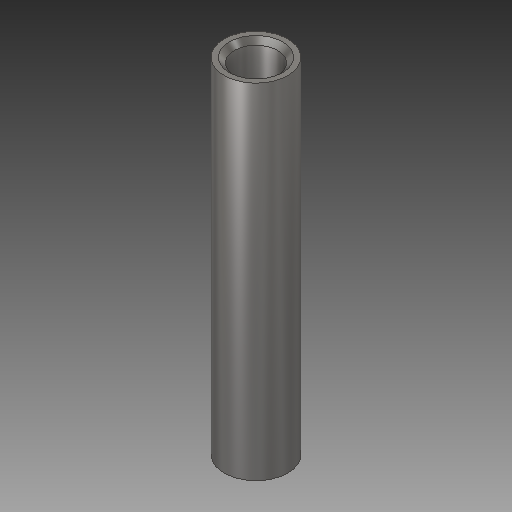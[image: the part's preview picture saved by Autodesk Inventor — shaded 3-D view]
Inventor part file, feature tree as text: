
AUTODESK INVENTOR PART (.ipt)
format: ipt  version: 2018.2 (Build 222227000, 227)  size: 106,496 bytes
history: native  units: mm
features: extrude x1, chamfer x1, sketch x1
ambient origin geometry x8: Origin, YZ Plane, XZ Plane, XY Plane, X Axis, Y Axis, Z Axis, Center Point
bodies: Solid1 (feature_tree)
feature tree (3):
  extrude  "Extrusion1"  Depth=52.0mm
  chamfer  "Chamfer1"  Distance=52.0mm
  sketch  "Sketch1"  dims[d0=6.55mm d1=9.6mm d2=52.0mm d3=0.0mm d4=0.75mm d5=2.0mm d6=45.0deg]
